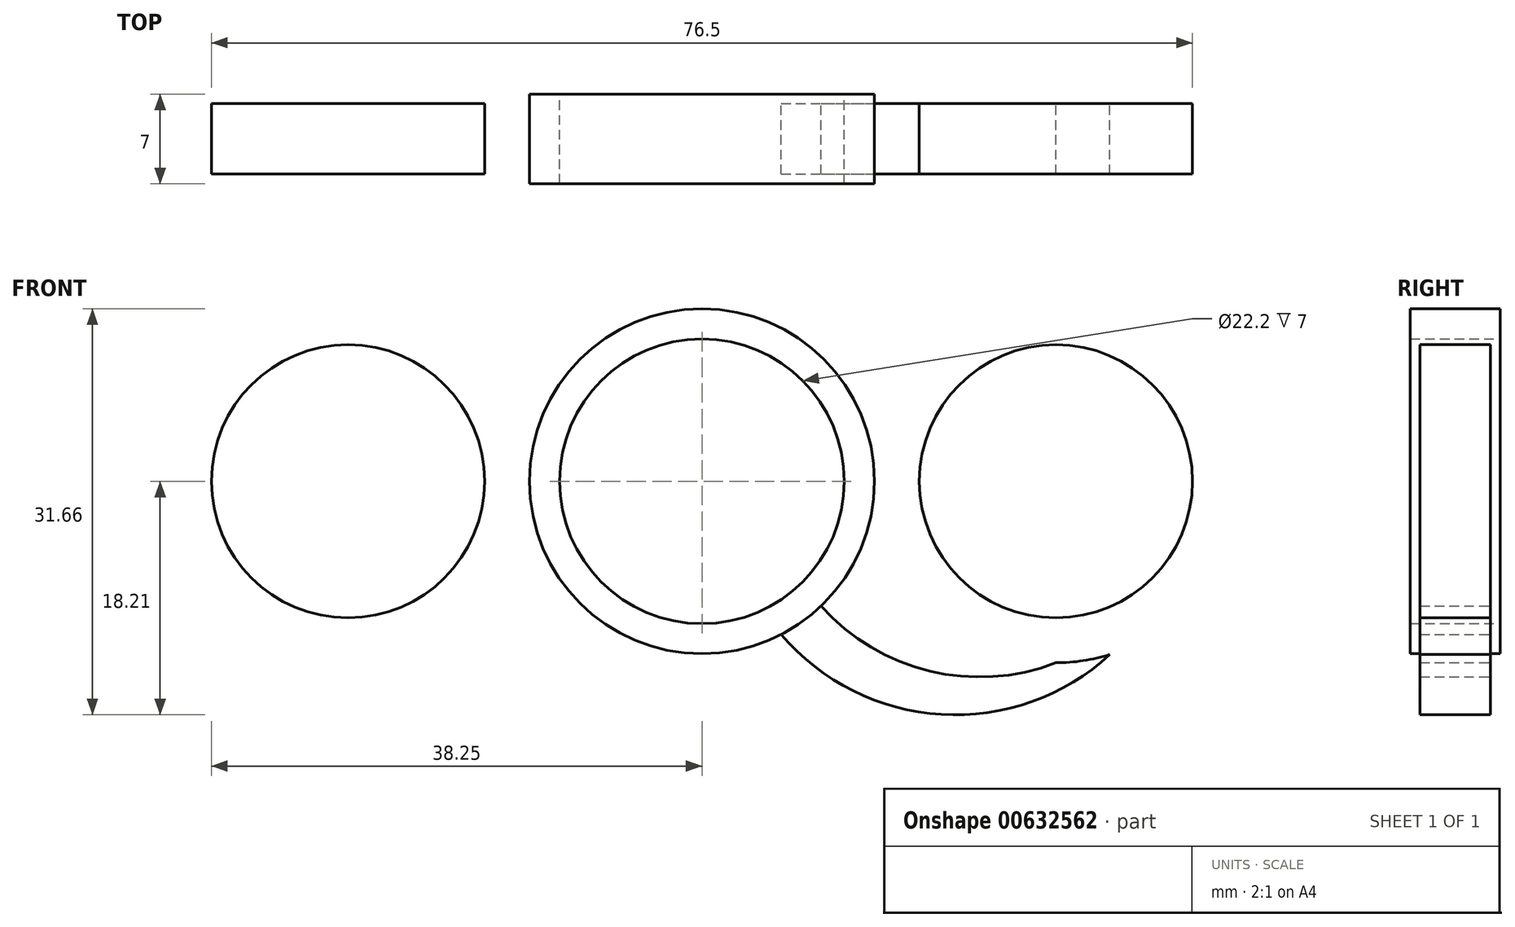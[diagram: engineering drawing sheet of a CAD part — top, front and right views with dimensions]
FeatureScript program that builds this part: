
annotation { "Feature Type Name" : "Feature", "Feature Type Description" : "" }
export const myFeature = defineFeature(function(context is Context, id is Id, definition is map)
    precondition{}
    {
        {
            var Q0;
            Q0=qCreatedBy(makeId("Front.planeOp"),FACE);
            var sketch = newSketch(context, id + "F0", { "sketchPlane" : qUnion([Q0])});
            skCircle(sketch, "E0", {"center": v(0, 0) * mm, "radius": 11.1 * mm});
            skCircle(sketch, "E1", {"center": v(0, 0) * mm, "radius": 13.45 * mm});
            skCircle(sketch, "E2", {"center": v(27.6, 0) * mm, "radius": 10.65 * mm});
            skCircle(sketch, "E3", {"center": v(27.6, 0) * mm, "radius": 14.15 * mm});
            skLineSegment(sketch, "E4", {"start": v(27.6, 0) * mm, "end": v(27.6, -14.15) * mm, "construction": true});
            skArc(sketch, "E5", {"start": v(9.29, -9.72) * mm, "mid": v(17.75, -14.8) * mm, "end": v(27.6, -14.15) * mm});
            skArc(sketch, "E6", {"start": v(6.17, -11.94) * mm, "mid": v(18.66, -18.18) * mm, "end": v(31.82, -13.5) * mm});
            skSolve(sketch);
        }
        {
            var Q0;
            Q0=qCreatedBy(makeId("Top.planeOp"),FACE);
            var sketch = newSketch(context, id + "F1", { "sketchPlane" : qUnion([Q0])});
            skSolve(sketch);
        }
        {
            var Q0;
            Q0=makeQuery(id+"F0.imprint","IMPRINT",FACE,{"disambiguationData":[TD([[makeQuery(id+"F0.imprint","IMPRINT",EDGE,{"derivedFrom":sQuery(id+"F0.wireOp",EDGE,"E0")}),-1.0]])]});
            extrude(context, id + "F2", {"entities" : qUnion([Q0]), "endBound" : BoundingType.SYMMETRIC, "depth" : 7 * mm, "offsetDistance" : 25 * mm});
        }
        {
            var Q0;
            Q0 = qSketchRegion(id + "F1", true);
            var Q1;
            Q1=makeQuery(id+"F0.imprint","IMPRINT",FACE,{"disambiguationData":[TD([[makeQuery(id+"F0.imprint","IMPRINT",EDGE,{"derivedFrom":sQuery(id+"F0.wireOp",EDGE,"E2")}),1.0]])]});
            extrude(context, id + "F3", {"entities" : qUnion([Q0, Q1]), "operationType" : NewBodyOperationType.ADD, "endBound" : BoundingType.SYMMETRIC, "depth" : 5.5 * mm, "offsetDistance" : 25 * mm});
        }
        {
            var Q0;
            {var subQ0=sQuery(id+"F0.wireOp",EDGE,"E5");Q0=makeQuery(id+"F0.imprint","IMPRINT",FACE,{"disambiguationData":[TD([[makeQuery(id+"F0.imprint","IMPRINT",EDGE,{"derivedFrom":subQ0}),-1.0]])]});}
            extrude(context, id + "F4", {"entities" : qUnion([Q0]), "endBound" : BoundingType.SYMMETRIC, "depth" : 5.5 * mm, "offsetDistance" : 25 * mm});
        }
        {
            var Q0;
            Q0=qCreatedBy(makeId("Top.planeOp"),FACE);
            var sketch = newSketch(context, id + "F5", { "sketchPlane" : qUnion([Q0])});
            skLineSegment(sketch, "E7", {"start": v(0, 0) * mm, "end": v(0, 21.24) * mm});
            skSolve(sketch);
        }
        {
            var Q0;
            Q0=makeQuery(id+"F3.opExtrude","SWEPT_BODY",BODY,{"disambiguationData":[OSD([sQuery(id+"F0.wireOp",EDGE,"E2"),sQuery(id+"F0.wireOp",EDGE,"E3")])]});
            var Q1;
            Q1=sQuery(id+"F5.wireOp",EDGE,"E7");
            circularPattern(context, id + "F6", {"entities" : qUnion([Q0]), "axis" : qUnion([Q1]), "angle" : 360 * degree, "instanceCount" : 2, "equalSpace" : true});
        }
    });
